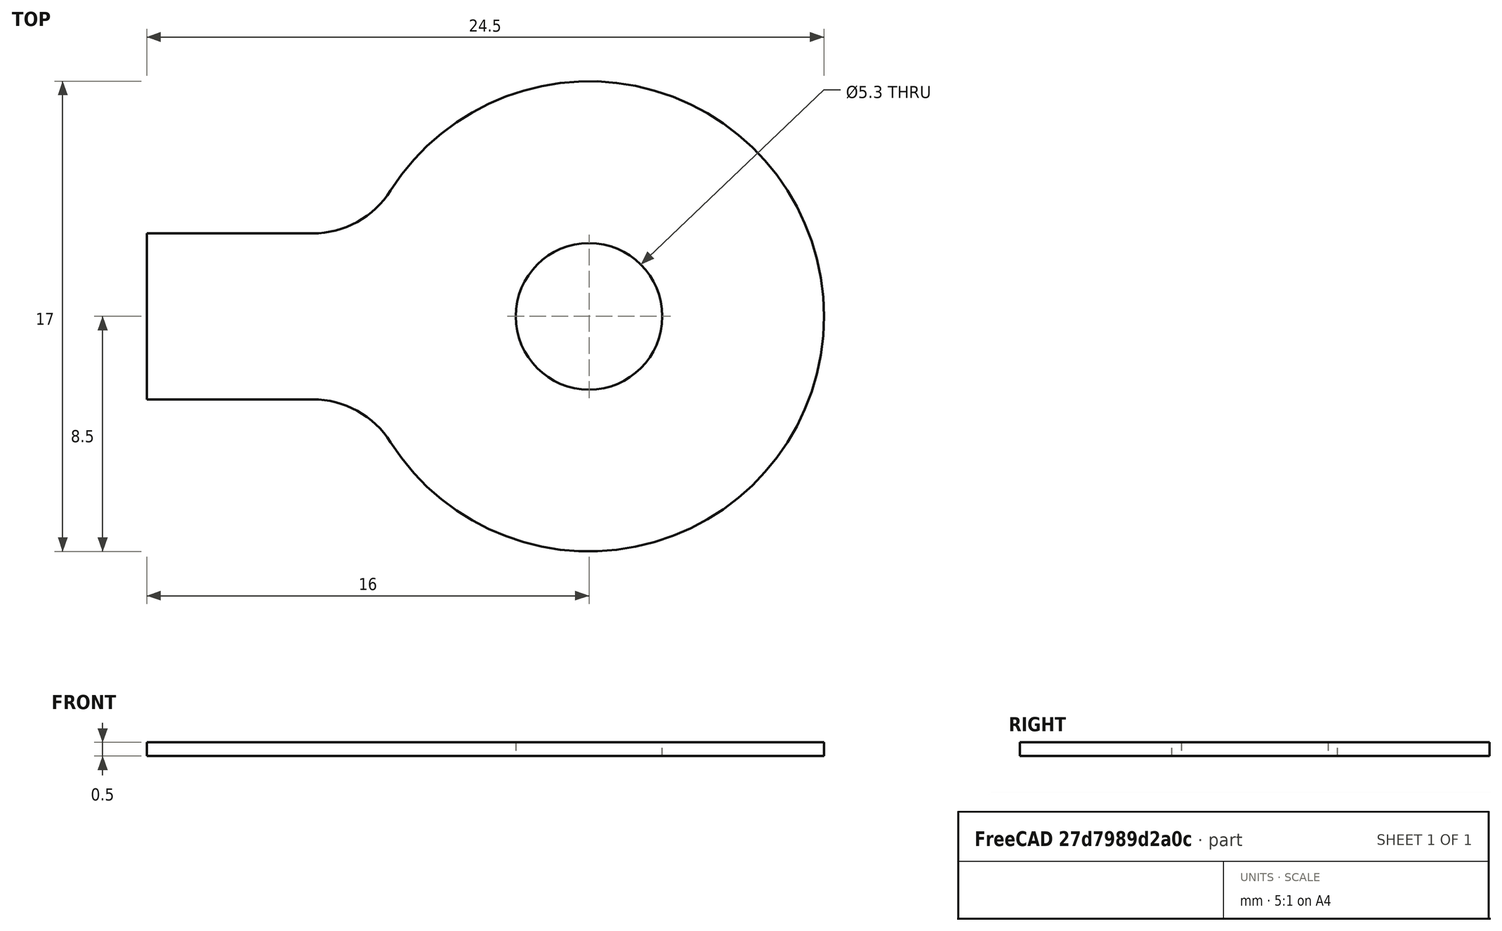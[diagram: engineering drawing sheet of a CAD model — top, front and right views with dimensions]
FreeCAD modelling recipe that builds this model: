
FCSTD DOCUMENT  (FreeCAD 0.15R4671 (Git))
Label: DIN93_M5TabWasher
License: CreativeCommons Attribution-ShareAlike
LicenseURL: http://creativecommons.org/licenses/by-sa/4.0/
objects: Sketcher::SketchObject×1, PartDesign::Pad×1
note: 3 computed .brp shape members not serialized (recipe doc carries the construction recipe); baked Part::Feature solids carry a one-line shape summary decoded from their .brp

FEATURE [Sketcher::SketchObject] Sketch
  sketch-geometry (7):
    g0: Circle CenterX=0 CenterY=0 CenterZ=0 NormalX=0 NormalY=0 NormalZ=1 Radius=2.65
    g1: LineSegment StartX=-16 StartY=3 StartZ=0 EndX=-10 EndY=3 EndZ=0
    g2: LineSegment StartX=-10 StartY=-3 StartZ=0 EndX=-16 EndY=-3 EndZ=0
    g3: LineSegment StartX=-16 StartY=-3 StartZ=0 EndX=-16 EndY=3 EndZ=0
    g4: ArcOfCircle CenterX=0 CenterY=0 CenterZ=0 NormalX=0 NormalY=0 NormalZ=1 Radius=8.5 StartAngle=3.7067 EndAngle=8.85967
    g5: ArcOfCircle CenterX=-9.99999 CenterY=6.34089 CenterZ=0 NormalX=0 NormalY=0 NormalZ=1 Radius=3.34089 StartAngle=4.71239 EndAngle=5.71807
    g6: ArcOfCircle CenterX=-9.99999 CenterY=-6.34089 CenterZ=0 NormalX=0 NormalY=0 NormalZ=1 Radius=3.34089 StartAngle=0.565116 EndAngle=1.5708
  constraints (22):
    c: Coincident(g0,g-1)
    c: Radius(g0) = 2.65
    c: Coincident(g2,g3)
    c: Coincident(g3,g1)
    c: Horizontal(g1)
    c: Horizontal(g2)
    c: Vertical(g3)
    c: Symmetric(g1,g2,g-1)
    c: Equal(g1,g3)
    c: Equal(g3,g2)
    c: DistanceY(g3) = 6
    c: DistanceX(g-1,g2) = -16
    c: Coincident(g4,g-1)
    c: Radius(g4) = 8.5
    c: Coincident(g5,g4)
    c: Coincident(g5,g1)
    c: Tangent(g5,g4)
    c: Coincident(g6,g2)
    c: Coincident(g6,g4)
    c: Tangent(g4,g6)
    c: Tangent(g6,g2)
    c: Tangent(g1,g5)
FEATURE [PartDesign::Pad] Pad
  Length = 0.5
  Length2 = 100
  Sketch = -> Sketch
  Type = 0
